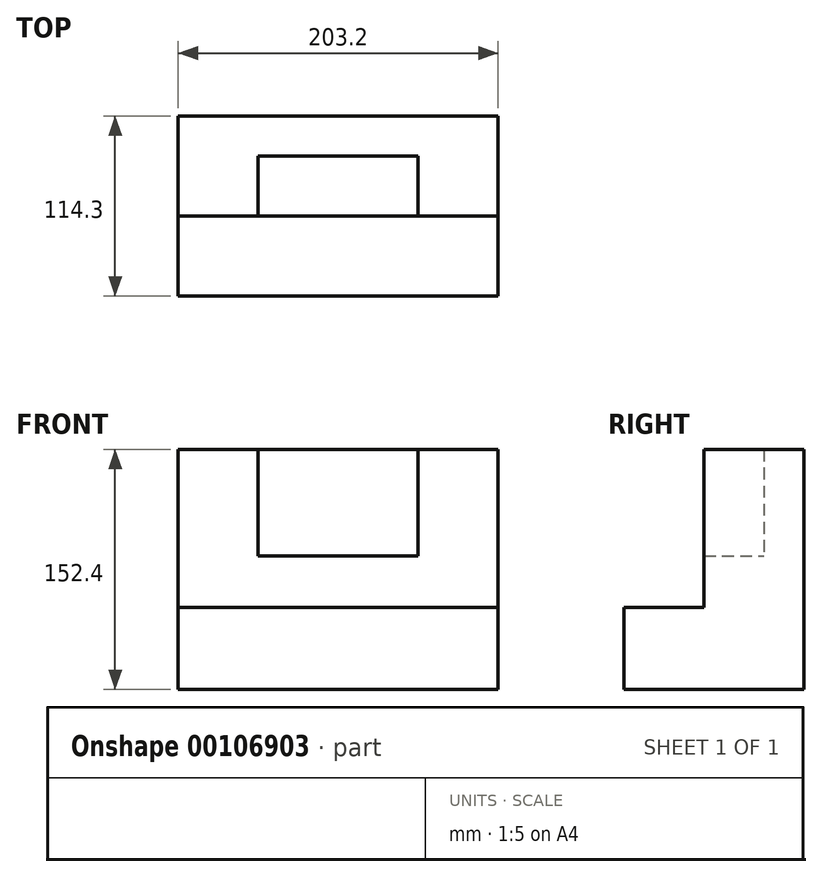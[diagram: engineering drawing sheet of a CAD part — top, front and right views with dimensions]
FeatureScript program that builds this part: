
annotation { "Feature Type Name" : "Feature", "Feature Type Description" : "" }
export const myFeature = defineFeature(function(context is Context, id is Id, definition is map)
    precondition{}
    {
        {
            var Q0;
            Q0=qCreatedBy(makeId("Front.planeOp"),FACE);
            var sketch = newSketch(context, id + "F0", { "sketchPlane" : qUnion([Q0])});
            skLineSegment(sketch, "E0", {"start": v(-80.07, 100.43) * mm, "end": v(-80.07, -51.97) * mm});
            skLineSegment(sketch, "E1", {"start": v(-80.07, -51.97) * mm, "end": v(123.13, -51.97) * mm});
            skLineSegment(sketch, "E2", {"start": v(123.13, -51.97) * mm, "end": v(123.13, 100.43) * mm});
            skLineSegment(sketch, "E3", {"start": v(-80.07, 100.43) * mm, "end": v(123.13, 100.43) * mm});
            skSolve(sketch);
        }
        {
            var Q0;
            Q0 = qSketchRegion(id + "F0", true);
            extrude(context, id + "F1", {"entities" : qUnion([Q0]), "depth" : 25.4 * mm});
        }
        {
            var Q0;
            Q0=makeQuery(id+"F1.opExtrude","CAP_FACE",FACE,{"disambiguationData":[OSD([sQuery(id+"F0.wireOp",EDGE,"E0"),sQuery(id+"F0.wireOp",EDGE,"E1"),sQuery(id+"F0.wireOp",EDGE,"E2"),sQuery(id+"F0.wireOp",EDGE,"E3")])],"isStart":false});
            var sketch = newSketch(context, id + "F2", { "sketchPlane" : qUnion([Q0])});
            skLineSegment(sketch, "E4", {"start": v(-29.27, 100.43) * mm, "end": v(-29.27, 32.68) * mm});
            skLineSegment(sketch, "E5", {"start": v(-29.27, 32.68) * mm, "end": v(72.33, 32.68) * mm});
            skLineSegment(sketch, "E6", {"start": v(72.33, 32.68) * mm, "end": v(72.33, 100.43) * mm});
            skLineSegment(sketch, "E7", {"start": v(72.33, 100.43) * mm, "end": v(123.13, 100.43) * mm});
            skLineSegment(sketch, "E8", {"start": v(-80.07, 100.43) * mm, "end": v(-29.27, 100.43) * mm});
            skLineSegment(sketch, "E9", {"start": v(-80.07, 100.43) * mm, "end": v(-80.07, -51.97) * mm});
            skLineSegment(sketch, "E10", {"start": v(-80.07, -51.97) * mm, "end": v(123.13, -51.97) * mm});
            skLineSegment(sketch, "E11", {"start": v(123.13, -51.97) * mm, "end": v(123.13, 100.43) * mm});
            skSolve(sketch);
        }
        {
            var Q0;
            Q0 = qSketchRegion(id + "F2", true);
            var Q1;
            Q1 = qSketchRegion(id + "F4", true);
            extrude(context, id + "F3", {"entities" : qUnion([Q0, Q1]), "operationType" : NewBodyOperationType.ADD, "depth" : 38.1 * mm});
        }
        {
            var Q0;
            Q0=makeQuery(id+"F3.opExtrude","CAP_FACE",FACE,{"disambiguationData":[OSD([sQuery(id+"F2.wireOp",EDGE,"E4"),sQuery(id+"F2.wireOp",EDGE,"E5"),sQuery(id+"F2.wireOp",EDGE,"E6"),sQuery(id+"F2.wireOp",EDGE,"E7"),sQuery(id+"F2.wireOp",EDGE,"E8"),sQuery(id+"F2.wireOp",EDGE,"E9"),sQuery(id+"F2.wireOp",EDGE,"E10"),sQuery(id+"F2.wireOp",EDGE,"E11")])],"isStart":false});
            var sketch = newSketch(context, id + "F4", { "sketchPlane" : qUnion([Q0])});
            skLineSegment(sketch, "E12", {"start": v(-80.07, -51.97) * mm, "end": v(123.13, -51.97) * mm});
            skLineSegment(sketch, "E13", {"start": v(123.13, -51.97) * mm, "end": v(123.13, 0) * mm});
            skLineSegment(sketch, "E14", {"start": v(123.13, 0) * mm, "end": v(-80.07, 0) * mm});
            skLineSegment(sketch, "E15", {"start": v(-80.07, 0) * mm, "end": v(-80.07, -51.97) * mm});
            skSolve(sketch);
        }
        {
            var Q0;
            Q0 = qSketchRegion(id + "F4", true);
            extrude(context, id + "F5", {"entities" : qUnion([Q0]), "operationType" : NewBodyOperationType.ADD, "depth" : 50.8 * mm});
        }
    });
